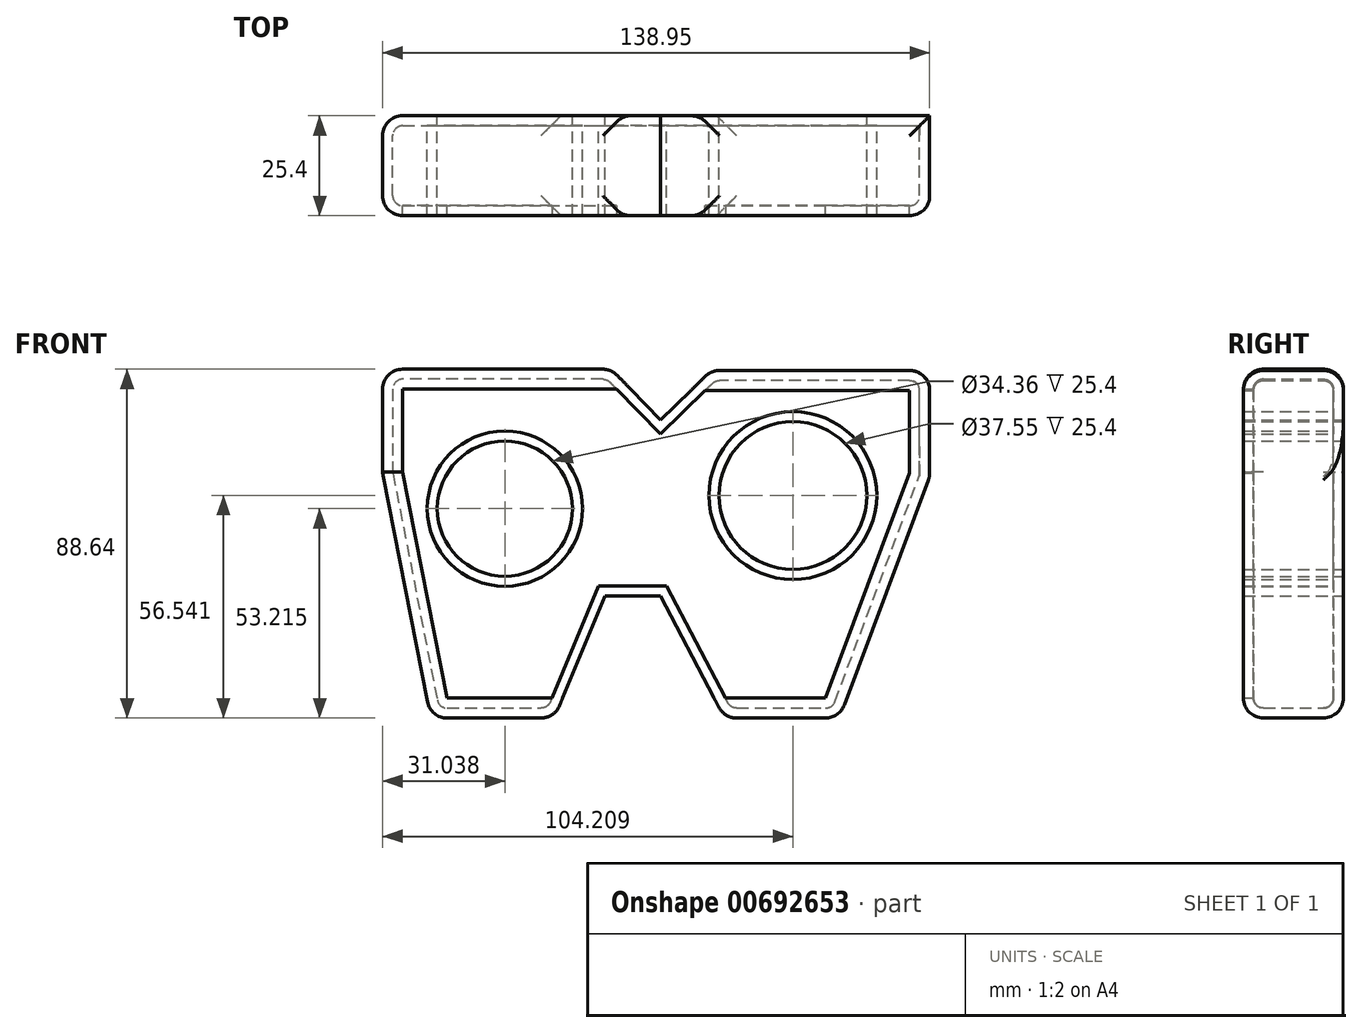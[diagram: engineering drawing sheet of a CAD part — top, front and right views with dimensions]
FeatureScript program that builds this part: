
annotation { "Feature Type Name" : "Feature", "Feature Type Description" : "" }
export const myFeature = defineFeature(function(context is Context, id is Id, definition is map)
    precondition{}
    {
        {
            var Q0;
            Q0=qCreatedBy(makeId("Front.planeOp"),FACE);
            var sketch = newSketch(context, id + "F0", { "sketchPlane" : qUnion([Q0])});
            skCircle(sketch, "E0", {"center": v(-39.54, 53.22) * mm, "radius": 17.18 * mm});
            skCircle(sketch, "E1", {"center": v(33.63, 56.54) * mm, "radius": 18.77 * mm});
            skLineSegment(sketch, "E2", {"start": v(-70.58, 62.08) * mm, "end": v(-58.39, 0) * mm});
            skLineSegment(sketch, "E3", {"start": v(-58.39, 0) * mm, "end": v(-26.98, 0) * mm});
            skLineSegment(sketch, "E4", {"start": v(-26.98, 0) * mm, "end": v(-14.04, 31.04) * mm});
            skLineSegment(sketch, "E5", {"start": v(-14.04, 31.04) * mm, "end": v(0, 31.04) * mm});
            skLineSegment(sketch, "E6", {"start": v(0, 31.04) * mm, "end": v(16.26, 0) * mm});
            skLineSegment(sketch, "E7", {"start": v(16.26, 0) * mm, "end": v(45.45, 0) * mm});
            skLineSegment(sketch, "E8", {"start": v(45.45, 0) * mm, "end": v(68.37, 61.35) * mm});
            skLineSegment(sketch, "E9", {"start": v(68.37, 61.35) * mm, "end": v(68.37, 88.32) * mm});
            skLineSegment(sketch, "E10", {"start": v(68.37, 88.32) * mm, "end": v(12.93, 88.32) * mm});
            skLineSegment(sketch, "E11", {"start": v(12.93, 88.32) * mm, "end": v(0, 75.76) * mm});
            skLineSegment(sketch, "E12", {"start": v(0, 75.76) * mm, "end": v(-12.52, 88.64) * mm});
            skLineSegment(sketch, "E13", {"start": v(-12.52, 88.64) * mm, "end": v(-70.58, 88.64) * mm});
            skLineSegment(sketch, "E14", {"start": v(-70.58, 88.64) * mm, "end": v(-70.58, 62.08) * mm});
            skSolve(sketch);
        }
        {
            var Q0;
            Q0=makeQuery(id+"F0.imprint","IMPRINT",FACE,{"disambiguationData":[TD([[makeQuery(id+"F0.imprint","IMPRINT",EDGE,{"derivedFrom":sQuery(id+"F0.wireOp",EDGE,"E0")}),-1.0]])]});
            extrude(context, id + "F1", {"entities" : qUnion([Q0]), "depth" : 25.4 * mm, "offsetDistance" : 25.4 * mm});
        }
        {
            var Q0;
            Q0=makeQuery(id+"F1.opExtrude","SWEPT_EDGE",EDGE,{"disambiguationData":[OSD([sQuery(id+"F0.wireOp",EDGE,"E13"),sQuery(id+"F0.wireOp",EDGE,"E14")])]});
            fillet(context, id + "F2", {"entities" : qUnion([Q0]), "radius" : 5.08 * mm, "tangentPropagation" : true, "allowEdgeOverflow" : false});
        }
        {
            var Q0;
            Q0=makeQuery(id+"F1.opExtrude","SWEPT_EDGE",EDGE,{"disambiguationData":[OSD([sQuery(id+"F0.wireOp",EDGE,"E9"),sQuery(id+"F0.wireOp",EDGE,"E10")])]});
            var Q1;
            Q1=makeQuery(id+"F1.opExtrude","CAP_EDGE",EDGE,{"disambiguationData":[OSD([sQuery(id+"F0.wireOp",EDGE,"E10")])],"isStart":false});
            var Q2;
            Q2=makeQuery(id+"F1.opExtrude","SWEPT_FACE",FACE,{"disambiguationData":[OSD([sQuery(id+"F0.wireOp",EDGE,"E13")])]});
            var Q3;
            Q3=makeQuery(id+"F1.opExtrude","SWEPT_FACE",FACE,{"disambiguationData":[OSD([sQuery(id+"F0.wireOp",EDGE,"E10")])]});
            fillet(context, id + "F3", {"entities" : qUnion([Q0, Q1, Q2, Q3]), "radius" : 5.08 * mm, "tangentPropagation" : true, "allowEdgeOverflow" : false});
        }
        {
            var Q0;
            Q0=makeQuery(id+"F1.opExtrude","CAP_EDGE",EDGE,{"disambiguationData":[OSD([sQuery(id+"F0.wireOp",EDGE,"E2")])],"isStart":true});
            var Q1;
            Q1=makeQuery(id+"F1.opExtrude","SWEPT_FACE",FACE,{"disambiguationData":[OSD([sQuery(id+"F0.wireOp",EDGE,"E2")])]});
            var Q2;
            Q2=makeQuery(id+"F1.opExtrude","SWEPT_FACE",FACE,{"disambiguationData":[OSD([sQuery(id+"F0.wireOp",EDGE,"E3")])]});
            var Q3;
            Q3=makeQuery(id+"F1.opExtrude","SWEPT_FACE",FACE,{"disambiguationData":[OSD([sQuery(id+"F0.wireOp",EDGE,"E8")])]});
            var Q4;
            Q4=makeQuery(id+"F1.opExtrude","SWEPT_FACE",FACE,{"disambiguationData":[OSD([sQuery(id+"F0.wireOp",EDGE,"E7")])]});
            var Q5;
            Q5=makeQuery(id+"F1.opExtrude","CAP_EDGE",EDGE,{"disambiguationData":[OSD([sQuery(id+"F0.wireOp",EDGE,"E9")])],"isStart":false});
            var Q6;
            Q6=makeQuery(id+"F1.opExtrude","SWEPT_EDGE",EDGE,{"disambiguationData":[OSD([sQuery(id+"F0.wireOp",EDGE,"E8"),sQuery(id+"F0.wireOp",EDGE,"E9")])]});
            fillet(context, id + "F4", {"entities" : qUnion([Q0, Q1, Q2, Q3, Q4, Q5, Q6]), "radius" : 5.08 * mm, "tangentPropagation" : true, "allowEdgeOverflow" : false});
        }
        {
            var Q0;
            Q0=makeQuery(id+"F1.opExtrude","CAP_FACE",FACE,{"disambiguationData":[OSD([sQuery(id+"F0.wireOp",EDGE,"E0"),sQuery(id+"F0.wireOp",EDGE,"E1"),sQuery(id+"F0.wireOp",EDGE,"E2"),sQuery(id+"F0.wireOp",EDGE,"E3"),sQuery(id+"F0.wireOp",EDGE,"E4"),sQuery(id+"F0.wireOp",EDGE,"E5"),sQuery(id+"F0.wireOp",EDGE,"E6"),sQuery(id+"F0.wireOp",EDGE,"E7"),sQuery(id+"F0.wireOp",EDGE,"E8"),sQuery(id+"F0.wireOp",EDGE,"E9"),sQuery(id+"F0.wireOp",EDGE,"E10"),sQuery(id+"F0.wireOp",EDGE,"E11"),sQuery(id+"F0.wireOp",EDGE,"E12"),sQuery(id+"F0.wireOp",EDGE,"E13"),sQuery(id+"F0.wireOp",EDGE,"E14")])],"isStart":false});
            shell(context, id + "F5", {"entities" : qUnion([Q0]), "thickness" : 2.54 * mm});
        }
    });
